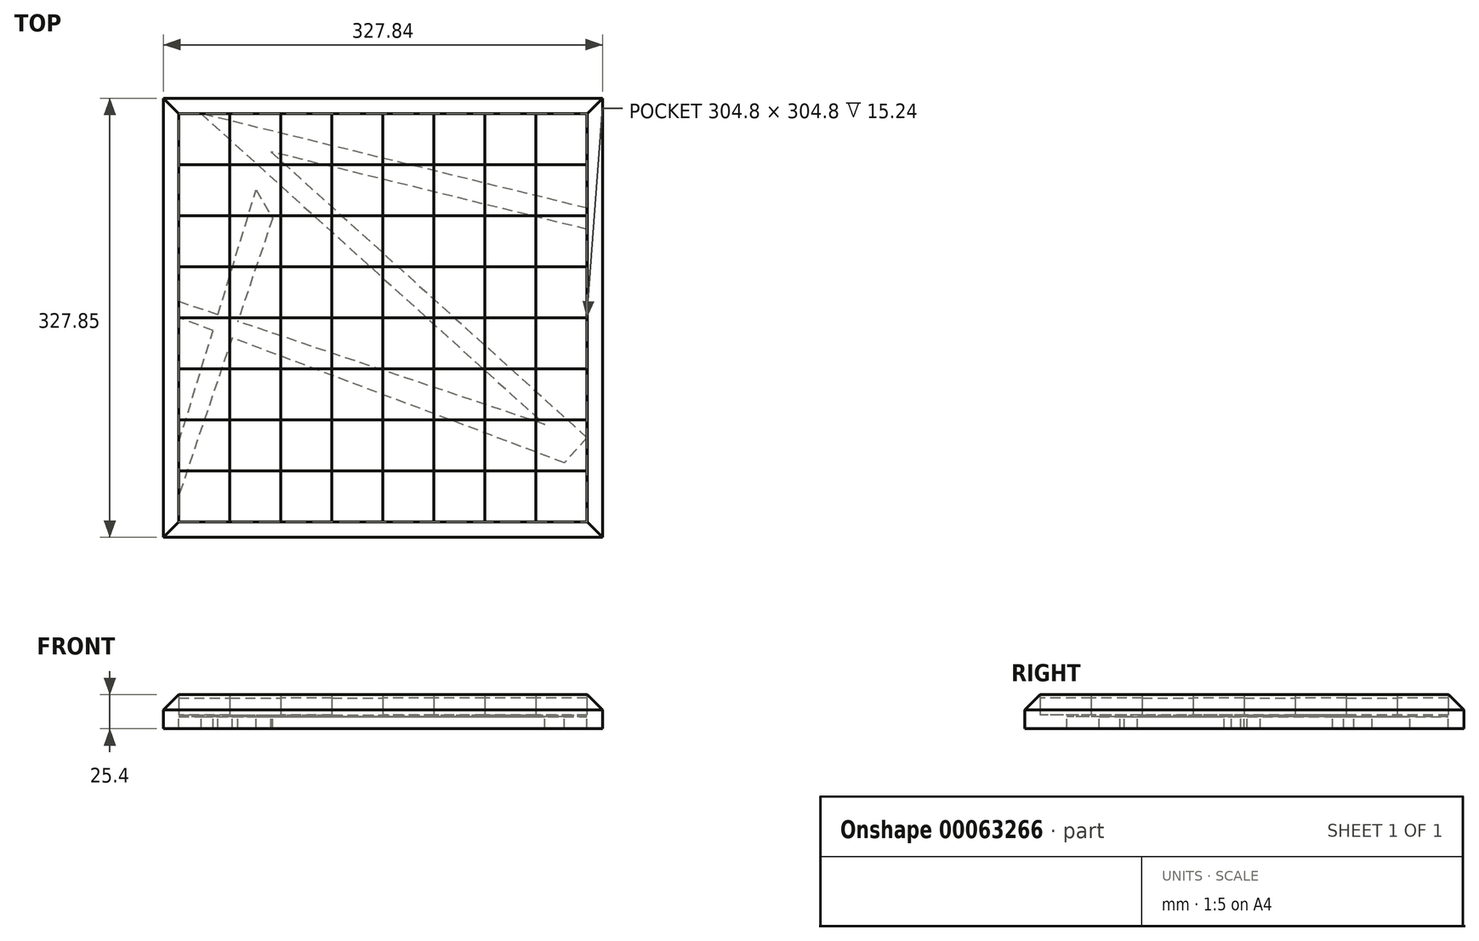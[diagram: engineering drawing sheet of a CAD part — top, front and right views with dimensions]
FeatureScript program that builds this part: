
annotation { "Feature Type Name" : "Feature", "Feature Type Description" : "" }
export const myFeature = defineFeature(function(context is Context, id is Id, definition is map)
    precondition{}
    {
        {
            var Q0;
            Q0=qCreatedBy(makeId("Top.planeOp"),FACE);
            var sketch = newSketch(context, id + "F0", { "sketchPlane" : qUnion([Q0])});
            skLineSegment(sketch, "E0", {"start": v(-203.2, 101.88) * mm, "end": v(101.6, 101.88) * mm});
            skLineSegment(sketch, "E1", {"start": v(101.6, 101.88) * mm, "end": v(101.6, -202.92) * mm});
            skLineSegment(sketch, "E2", {"start": v(101.6, -202.92) * mm, "end": v(-203.2, -202.92) * mm});
            skLineSegment(sketch, "E3", {"start": v(-203.2, -202.92) * mm, "end": v(-203.2, 101.88) * mm});
            skLineSegment(sketch, "E4", {"start": v(-165.1, 101.88) * mm, "end": v(-165.1, -202.92) * mm});
            skLineSegment(sketch, "E5", {"start": v(-127, -202.92) * mm, "end": v(-127, 101.88) * mm});
            skLineSegment(sketch, "E6", {"start": v(-88.9, 101.88) * mm, "end": v(-88.9, -202.92) * mm});
            skLineSegment(sketch, "E7", {"start": v(-50.8, 101.88) * mm, "end": v(-50.8, -202.92) * mm});
            skLineSegment(sketch, "E8", {"start": v(-12.7, -202.92) * mm, "end": v(-12.7, 101.88) * mm});
            skLineSegment(sketch, "E9", {"start": v(25.4, -202.92) * mm, "end": v(25.4, 101.88) * mm});
            skLineSegment(sketch, "E10", {"start": v(63.5, 101.88) * mm, "end": v(63.5, -202.92) * mm});
            skLineSegment(sketch, "E11", {"start": v(-203.2, 63.78) * mm, "end": v(101.6, 63.78) * mm});
            skLineSegment(sketch, "E12", {"start": v(-203.2, 25.68) * mm, "end": v(101.6, 25.68) * mm});
            skLineSegment(sketch, "E13", {"start": v(-203.2, -12.42) * mm, "end": v(101.6, -12.42) * mm});
            skLineSegment(sketch, "E14", {"start": v(101.6, -50.52) * mm, "end": v(-203.2, -50.52) * mm});
            skLineSegment(sketch, "E15", {"start": v(-203.2, -88.62) * mm, "end": v(101.6, -88.62) * mm});
            skLineSegment(sketch, "E16", {"start": v(101.6, -126.72) * mm, "end": v(-203.2, -126.72) * mm});
            skLineSegment(sketch, "E17", {"start": v(101.6, -164.82) * mm, "end": v(-203.2, -164.82) * mm});
            skSolve(sketch);
        }
        {
            var Q0;
            {var subQ0=sQuery(id+"F0.wireOp",EDGE,"E3");var subQ1=sQuery(id+"F0.wireOp",EDGE,"E0");var subQ2=makeQuery(id+"F0.imprint","INTERSECT",VERTEX,{"derivedFrom":[subQ1,subQ0]});Q0=makeQuery(id+"F0.imprint","IMPRINT",FACE,{"disambiguationData":[TD([[makeQuery(id+"F0.imprint","IMPRINT",EDGE,{"disambiguationData":[TD([[subQ2,-1.0]])],"derivedFrom":subQ1}),-1.0]])]});}
            var Q1;
            {var subQ0=sQuery(id+"F0.wireOp",EDGE,"E11");var subQ1=sQuery(id+"F0.wireOp",EDGE,"E4");var subQ2=makeQuery(id+"F0.imprint","INTERSECT",VERTEX,{"derivedFrom":[subQ1,subQ0]});Q1=makeQuery(id+"F0.imprint","IMPRINT",FACE,{"disambiguationData":[TD([[makeQuery(id+"F0.imprint","IMPRINT",EDGE,{"disambiguationData":[TD([[subQ2,-1.0]])],"derivedFrom":subQ1}),1.0]])]});}
            var Q2;
            {var subQ0=sQuery(id+"F0.wireOp",EDGE,"E5");var subQ1=sQuery(id+"F0.wireOp",EDGE,"E0");var subQ2=makeQuery(id+"F0.imprint","INTERSECT",VERTEX,{"derivedFrom":[subQ1,subQ0]});Q2=makeQuery(id+"F0.imprint","IMPRINT",FACE,{"disambiguationData":[TD([[makeQuery(id+"F0.imprint","IMPRINT",EDGE,{"disambiguationData":[TD([[subQ2,-1.0]])],"derivedFrom":subQ1}),-1.0]])]});}
            var Q3;
            {var subQ0=sQuery(id+"F0.wireOp",EDGE,"E11");var subQ1=sQuery(id+"F0.wireOp",EDGE,"E6");var subQ2=makeQuery(id+"F0.imprint","INTERSECT",VERTEX,{"derivedFrom":[subQ1,subQ0]});Q3=makeQuery(id+"F0.imprint","IMPRINT",FACE,{"disambiguationData":[TD([[makeQuery(id+"F0.imprint","IMPRINT",EDGE,{"disambiguationData":[TD([[subQ2,-1.0]])],"derivedFrom":subQ1}),1.0]])]});}
            var Q4;
            {var subQ0=sQuery(id+"F0.wireOp",EDGE,"E7");var subQ1=sQuery(id+"F0.wireOp",EDGE,"E0");var subQ2=makeQuery(id+"F0.imprint","INTERSECT",VERTEX,{"derivedFrom":[subQ1,subQ0]});Q4=makeQuery(id+"F0.imprint","IMPRINT",FACE,{"disambiguationData":[TD([[makeQuery(id+"F0.imprint","IMPRINT",EDGE,{"disambiguationData":[TD([[subQ2,-1.0]])],"derivedFrom":subQ1}),-1.0]])]});}
            var Q5;
            {var subQ0=sQuery(id+"F0.wireOp",EDGE,"E12");var subQ1=sQuery(id+"F0.wireOp",EDGE,"E8");var subQ2=makeQuery(id+"F0.imprint","INTERSECT",VERTEX,{"derivedFrom":[subQ1,subQ0]});Q5=makeQuery(id+"F0.imprint","IMPRINT",FACE,{"disambiguationData":[TD([[makeQuery(id+"F0.imprint","IMPRINT",EDGE,{"disambiguationData":[TD([[subQ2,-1.0]])],"derivedFrom":subQ1}),-1.0]])]});}
            var Q6;
            {var subQ0=sQuery(id+"F0.wireOp",EDGE,"E9");var subQ1=sQuery(id+"F0.wireOp",EDGE,"E0");var subQ2=makeQuery(id+"F0.imprint","INTERSECT",VERTEX,{"derivedFrom":[subQ1,subQ0]});Q6=makeQuery(id+"F0.imprint","IMPRINT",FACE,{"disambiguationData":[TD([[makeQuery(id+"F0.imprint","IMPRINT",EDGE,{"disambiguationData":[TD([[subQ2,-1.0]])],"derivedFrom":subQ1}),-1.0]])]});}
            var Q7;
            {var subQ0=sQuery(id+"F0.wireOp",EDGE,"E11");var subQ1=sQuery(id+"F0.wireOp",EDGE,"E1");var subQ2=makeQuery(id+"F0.imprint","INTERSECT",VERTEX,{"derivedFrom":[subQ1,subQ0]});Q7=makeQuery(id+"F0.imprint","IMPRINT",FACE,{"disambiguationData":[TD([[makeQuery(id+"F0.imprint","IMPRINT",EDGE,{"disambiguationData":[TD([[subQ2,-1.0]])],"derivedFrom":subQ1}),-1.0]])]});}
            var Q8;
            {var subQ0=sQuery(id+"F0.wireOp",EDGE,"E12");var subQ1=sQuery(id+"F0.wireOp",EDGE,"E3");var subQ2=makeQuery(id+"F0.imprint","INTERSECT",VERTEX,{"derivedFrom":[subQ1,subQ0]});Q8=makeQuery(id+"F0.imprint","IMPRINT",FACE,{"disambiguationData":[TD([[makeQuery(id+"F0.imprint","IMPRINT",EDGE,{"disambiguationData":[TD([[subQ2,1.0]])],"derivedFrom":subQ1}),-1.0]])]});}
            var Q9;
            {var subQ0=sQuery(id+"F0.wireOp",EDGE,"E13");var subQ1=sQuery(id+"F0.wireOp",EDGE,"E4");var subQ2=makeQuery(id+"F0.imprint","INTERSECT",VERTEX,{"derivedFrom":[subQ1,subQ0]});Q9=makeQuery(id+"F0.imprint","IMPRINT",FACE,{"disambiguationData":[TD([[makeQuery(id+"F0.imprint","IMPRINT",EDGE,{"disambiguationData":[TD([[subQ2,-1.0]])],"derivedFrom":subQ1}),1.0]])]});}
            var Q10;
            {var subQ0=sQuery(id+"F0.wireOp",EDGE,"E13");var subQ1=sQuery(id+"F0.wireOp",EDGE,"E5");var subQ2=makeQuery(id+"F0.imprint","INTERSECT",VERTEX,{"derivedFrom":[subQ1,subQ0]});Q10=makeQuery(id+"F0.imprint","IMPRINT",FACE,{"disambiguationData":[TD([[makeQuery(id+"F0.imprint","IMPRINT",EDGE,{"disambiguationData":[TD([[subQ2,-1.0]])],"derivedFrom":subQ1}),-1.0]])]});}
            var Q11;
            {var subQ0=sQuery(id+"F0.wireOp",EDGE,"E13");var subQ1=sQuery(id+"F0.wireOp",EDGE,"E6");var subQ2=makeQuery(id+"F0.imprint","INTERSECT",VERTEX,{"derivedFrom":[subQ1,subQ0]});Q11=makeQuery(id+"F0.imprint","IMPRINT",FACE,{"disambiguationData":[TD([[makeQuery(id+"F0.imprint","IMPRINT",EDGE,{"disambiguationData":[TD([[subQ2,-1.0]])],"derivedFrom":subQ1}),1.0]])]});}
            var Q12;
            {var subQ0=sQuery(id+"F0.wireOp",EDGE,"E12");var subQ1=sQuery(id+"F0.wireOp",EDGE,"E7");var subQ2=makeQuery(id+"F0.imprint","INTERSECT",VERTEX,{"derivedFrom":[subQ1,subQ0]});Q12=makeQuery(id+"F0.imprint","IMPRINT",FACE,{"disambiguationData":[TD([[makeQuery(id+"F0.imprint","IMPRINT",EDGE,{"disambiguationData":[TD([[subQ2,-1.0]])],"derivedFrom":subQ1}),1.0]])]});}
            var Q13;
            {var subQ0=sQuery(id+"F0.wireOp",EDGE,"E14");var subQ1=sQuery(id+"F0.wireOp",EDGE,"E8");var subQ2=makeQuery(id+"F0.imprint","INTERSECT",VERTEX,{"derivedFrom":[subQ1,subQ0]});Q13=makeQuery(id+"F0.imprint","IMPRINT",FACE,{"disambiguationData":[TD([[makeQuery(id+"F0.imprint","IMPRINT",EDGE,{"disambiguationData":[TD([[subQ2,-1.0]])],"derivedFrom":subQ1}),-1.0]])]});}
            var Q14;
            {var subQ0=sQuery(id+"F0.wireOp",EDGE,"E13");var subQ1=sQuery(id+"F0.wireOp",EDGE,"E9");var subQ2=makeQuery(id+"F0.imprint","INTERSECT",VERTEX,{"derivedFrom":[subQ1,subQ0]});Q14=makeQuery(id+"F0.imprint","IMPRINT",FACE,{"disambiguationData":[TD([[makeQuery(id+"F0.imprint","IMPRINT",EDGE,{"disambiguationData":[TD([[subQ2,-1.0]])],"derivedFrom":subQ1}),-1.0]])]});}
            var Q15;
            {var subQ0=sQuery(id+"F0.wireOp",EDGE,"E13");var subQ1=sQuery(id+"F0.wireOp",EDGE,"E1");var subQ2=makeQuery(id+"F0.imprint","INTERSECT",VERTEX,{"derivedFrom":[subQ1,subQ0]});Q15=makeQuery(id+"F0.imprint","IMPRINT",FACE,{"disambiguationData":[TD([[makeQuery(id+"F0.imprint","IMPRINT",EDGE,{"disambiguationData":[TD([[subQ2,-1.0]])],"derivedFrom":subQ1}),-1.0]])]});}
            var Q16;
            {var subQ0=sQuery(id+"F0.wireOp",EDGE,"E15");var subQ1=sQuery(id+"F0.wireOp",EDGE,"E9");var subQ2=makeQuery(id+"F0.imprint","INTERSECT",VERTEX,{"derivedFrom":[subQ1,subQ0]});Q16=makeQuery(id+"F0.imprint","IMPRINT",FACE,{"disambiguationData":[TD([[makeQuery(id+"F0.imprint","IMPRINT",EDGE,{"disambiguationData":[TD([[subQ2,-1.0]])],"derivedFrom":subQ1}),-1.0]])]});}
            var Q17;
            {var subQ0=sQuery(id+"F0.wireOp",EDGE,"E14");var subQ1=sQuery(id+"F0.wireOp",EDGE,"E7");var subQ2=makeQuery(id+"F0.imprint","INTERSECT",VERTEX,{"derivedFrom":[subQ1,subQ0]});Q17=makeQuery(id+"F0.imprint","IMPRINT",FACE,{"disambiguationData":[TD([[makeQuery(id+"F0.imprint","IMPRINT",EDGE,{"disambiguationData":[TD([[subQ2,-1.0]])],"derivedFrom":subQ1}),1.0]])]});}
            var Q18;
            {var subQ0=sQuery(id+"F0.wireOp",EDGE,"E15");var subQ1=sQuery(id+"F0.wireOp",EDGE,"E5");var subQ2=makeQuery(id+"F0.imprint","INTERSECT",VERTEX,{"derivedFrom":[subQ1,subQ0]});Q18=makeQuery(id+"F0.imprint","IMPRINT",FACE,{"disambiguationData":[TD([[makeQuery(id+"F0.imprint","IMPRINT",EDGE,{"disambiguationData":[TD([[subQ2,-1.0]])],"derivedFrom":subQ1}),-1.0]])]});}
            var Q19;
            {var subQ0=sQuery(id+"F0.wireOp",EDGE,"E14");var subQ1=sQuery(id+"F0.wireOp",EDGE,"E3");var subQ2=makeQuery(id+"F0.imprint","INTERSECT",VERTEX,{"derivedFrom":[subQ1,subQ0]});Q19=makeQuery(id+"F0.imprint","IMPRINT",FACE,{"disambiguationData":[TD([[makeQuery(id+"F0.imprint","IMPRINT",EDGE,{"disambiguationData":[TD([[subQ2,1.0]])],"derivedFrom":subQ1}),-1.0]])]});}
            var Q20;
            {var subQ0=sQuery(id+"F0.wireOp",EDGE,"E15");var subQ1=sQuery(id+"F0.wireOp",EDGE,"E4");var subQ2=makeQuery(id+"F0.imprint","INTERSECT",VERTEX,{"derivedFrom":[subQ1,subQ0]});Q20=makeQuery(id+"F0.imprint","IMPRINT",FACE,{"disambiguationData":[TD([[makeQuery(id+"F0.imprint","IMPRINT",EDGE,{"disambiguationData":[TD([[subQ2,-1.0]])],"derivedFrom":subQ1}),1.0]])]});}
            var Q21;
            {var subQ0=sQuery(id+"F0.wireOp",EDGE,"E15");var subQ1=sQuery(id+"F0.wireOp",EDGE,"E6");var subQ2=makeQuery(id+"F0.imprint","INTERSECT",VERTEX,{"derivedFrom":[subQ1,subQ0]});Q21=makeQuery(id+"F0.imprint","IMPRINT",FACE,{"disambiguationData":[TD([[makeQuery(id+"F0.imprint","IMPRINT",EDGE,{"disambiguationData":[TD([[subQ2,-1.0]])],"derivedFrom":subQ1}),1.0]])]});}
            var Q22;
            {var subQ0=sQuery(id+"F0.wireOp",EDGE,"E16");var subQ1=sQuery(id+"F0.wireOp",EDGE,"E8");var subQ2=makeQuery(id+"F0.imprint","INTERSECT",VERTEX,{"derivedFrom":[subQ1,subQ0]});Q22=makeQuery(id+"F0.imprint","IMPRINT",FACE,{"disambiguationData":[TD([[makeQuery(id+"F0.imprint","IMPRINT",EDGE,{"disambiguationData":[TD([[subQ2,-1.0]])],"derivedFrom":subQ1}),-1.0]])]});}
            var Q23;
            {var subQ0=sQuery(id+"F0.wireOp",EDGE,"E15");var subQ1=sQuery(id+"F0.wireOp",EDGE,"E1");var subQ2=makeQuery(id+"F0.imprint","INTERSECT",VERTEX,{"derivedFrom":[subQ1,subQ0]});Q23=makeQuery(id+"F0.imprint","IMPRINT",FACE,{"disambiguationData":[TD([[makeQuery(id+"F0.imprint","IMPRINT",EDGE,{"disambiguationData":[TD([[subQ2,-1.0]])],"derivedFrom":subQ1}),-1.0]])]});}
            var Q24;
            {var subQ0=sQuery(id+"F0.wireOp",EDGE,"E17");var subQ1=sQuery(id+"F0.wireOp",EDGE,"E9");var subQ2=makeQuery(id+"F0.imprint","INTERSECT",VERTEX,{"derivedFrom":[subQ1,subQ0]});Q24=makeQuery(id+"F0.imprint","IMPRINT",FACE,{"disambiguationData":[TD([[makeQuery(id+"F0.imprint","IMPRINT",EDGE,{"disambiguationData":[TD([[subQ2,-1.0]])],"derivedFrom":subQ1}),-1.0]])]});}
            var Q25;
            {var subQ0=sQuery(id+"F0.wireOp",EDGE,"E16");var subQ1=sQuery(id+"F0.wireOp",EDGE,"E7");var subQ2=makeQuery(id+"F0.imprint","INTERSECT",VERTEX,{"derivedFrom":[subQ1,subQ0]});Q25=makeQuery(id+"F0.imprint","IMPRINT",FACE,{"disambiguationData":[TD([[makeQuery(id+"F0.imprint","IMPRINT",EDGE,{"disambiguationData":[TD([[subQ2,-1.0]])],"derivedFrom":subQ1}),1.0]])]});}
            var Q26;
            {var subQ0=sQuery(id+"F0.wireOp",EDGE,"E17");var subQ1=sQuery(id+"F0.wireOp",EDGE,"E5");var subQ2=makeQuery(id+"F0.imprint","INTERSECT",VERTEX,{"derivedFrom":[subQ1,subQ0]});Q26=makeQuery(id+"F0.imprint","IMPRINT",FACE,{"disambiguationData":[TD([[makeQuery(id+"F0.imprint","IMPRINT",EDGE,{"disambiguationData":[TD([[subQ2,-1.0]])],"derivedFrom":subQ1}),-1.0]])]});}
            var Q27;
            {var subQ0=sQuery(id+"F0.wireOp",EDGE,"E16");var subQ1=sQuery(id+"F0.wireOp",EDGE,"E3");var subQ2=makeQuery(id+"F0.imprint","INTERSECT",VERTEX,{"derivedFrom":[subQ1,subQ0]});Q27=makeQuery(id+"F0.imprint","IMPRINT",FACE,{"disambiguationData":[TD([[makeQuery(id+"F0.imprint","IMPRINT",EDGE,{"disambiguationData":[TD([[subQ2,1.0]])],"derivedFrom":subQ1}),-1.0]])]});}
            var Q28;
            {var subQ0=sQuery(id+"F0.wireOp",EDGE,"E4");var subQ1=sQuery(id+"F0.wireOp",EDGE,"E2");var subQ2=makeQuery(id+"F0.imprint","INTERSECT",VERTEX,{"derivedFrom":[subQ1,subQ0]});Q28=makeQuery(id+"F0.imprint","IMPRINT",FACE,{"disambiguationData":[TD([[makeQuery(id+"F0.imprint","IMPRINT",EDGE,{"disambiguationData":[TD([[subQ2,1.0]])],"derivedFrom":subQ1}),-1.0]])]});}
            var Q29;
            {var subQ0=sQuery(id+"F0.wireOp",EDGE,"E6");var subQ1=sQuery(id+"F0.wireOp",EDGE,"E2");var subQ2=makeQuery(id+"F0.imprint","INTERSECT",VERTEX,{"derivedFrom":[subQ1,subQ0]});Q29=makeQuery(id+"F0.imprint","IMPRINT",FACE,{"disambiguationData":[TD([[makeQuery(id+"F0.imprint","IMPRINT",EDGE,{"disambiguationData":[TD([[subQ2,1.0]])],"derivedFrom":subQ1}),-1.0]])]});}
            var Q30;
            {var subQ0=sQuery(id+"F0.wireOp",EDGE,"E8");var subQ1=sQuery(id+"F0.wireOp",EDGE,"E2");var subQ2=makeQuery(id+"F0.imprint","INTERSECT",VERTEX,{"derivedFrom":[subQ1,subQ0]});Q30=makeQuery(id+"F0.imprint","IMPRINT",FACE,{"disambiguationData":[TD([[makeQuery(id+"F0.imprint","IMPRINT",EDGE,{"disambiguationData":[TD([[subQ2,1.0]])],"derivedFrom":subQ1}),-1.0]])]});}
            var Q31;
            {var subQ0=sQuery(id+"F0.wireOp",EDGE,"E2");var subQ1=sQuery(id+"F0.wireOp",EDGE,"E1");var subQ2=makeQuery(id+"F0.imprint","INTERSECT",VERTEX,{"derivedFrom":[subQ1,subQ0]});Q31=makeQuery(id+"F0.imprint","IMPRINT",FACE,{"disambiguationData":[TD([[makeQuery(id+"F0.imprint","IMPRINT",EDGE,{"disambiguationData":[TD([[subQ2,1.0]])],"derivedFrom":subQ1}),-1.0]])]});}
            extrude(context, id + "F1", {"entities" : qUnion([Q0, Q1, Q2, Q3, Q4, Q5, Q6, Q7, Q8, Q9, Q10, Q11, Q12, Q13, Q14, Q15, Q16, Q17, Q18, Q19, Q20, Q21, Q22, Q23, Q24, Q25, Q26, Q27, Q28, Q29, Q30, Q31]), "depth" : 12.7 * mm});
        }
        {
            var Q0;
            {var subQ0=sQuery(id+"F0.wireOp",EDGE,"E4");var subQ1=sQuery(id+"F0.wireOp",EDGE,"E0");var subQ2=makeQuery(id+"F0.imprint","INTERSECT",VERTEX,{"derivedFrom":[subQ1,subQ0]});Q0=makeQuery(id+"F0.imprint","IMPRINT",FACE,{"disambiguationData":[TD([[makeQuery(id+"F0.imprint","IMPRINT",EDGE,{"disambiguationData":[TD([[subQ2,-1.0]])],"derivedFrom":subQ1}),-1.0]])]});}
            var Q1;
            {var subQ0=sQuery(id+"F0.wireOp",EDGE,"E11");var subQ1=sQuery(id+"F0.wireOp",EDGE,"E3");var subQ2=makeQuery(id+"F0.imprint","INTERSECT",VERTEX,{"derivedFrom":[subQ1,subQ0]});Q1=makeQuery(id+"F0.imprint","IMPRINT",FACE,{"disambiguationData":[TD([[makeQuery(id+"F0.imprint","IMPRINT",EDGE,{"disambiguationData":[TD([[subQ2,1.0]])],"derivedFrom":subQ1}),-1.0]])]});}
            var Q2;
            {var subQ0=sQuery(id+"F0.wireOp",EDGE,"E12");var subQ1=sQuery(id+"F0.wireOp",EDGE,"E4");var subQ2=makeQuery(id+"F0.imprint","INTERSECT",VERTEX,{"derivedFrom":[subQ1,subQ0]});Q2=makeQuery(id+"F0.imprint","IMPRINT",FACE,{"disambiguationData":[TD([[makeQuery(id+"F0.imprint","IMPRINT",EDGE,{"disambiguationData":[TD([[subQ2,-1.0]])],"derivedFrom":subQ1}),1.0]])]});}
            var Q3;
            {var subQ0=sQuery(id+"F0.wireOp",EDGE,"E12");var subQ1=sQuery(id+"F0.wireOp",EDGE,"E5");var subQ2=makeQuery(id+"F0.imprint","INTERSECT",VERTEX,{"derivedFrom":[subQ1,subQ0]});Q3=makeQuery(id+"F0.imprint","IMPRINT",FACE,{"disambiguationData":[TD([[makeQuery(id+"F0.imprint","IMPRINT",EDGE,{"disambiguationData":[TD([[subQ2,-1.0]])],"derivedFrom":subQ1}),-1.0]])]});}
            var Q4;
            {var subQ0=sQuery(id+"F0.wireOp",EDGE,"E6");var subQ1=sQuery(id+"F0.wireOp",EDGE,"E0");var subQ2=makeQuery(id+"F0.imprint","INTERSECT",VERTEX,{"derivedFrom":[subQ1,subQ0]});Q4=makeQuery(id+"F0.imprint","IMPRINT",FACE,{"disambiguationData":[TD([[makeQuery(id+"F0.imprint","IMPRINT",EDGE,{"disambiguationData":[TD([[subQ2,-1.0]])],"derivedFrom":subQ1}),-1.0]])]});}
            var Q5;
            {var subQ0=sQuery(id+"F0.wireOp",EDGE,"E12");var subQ1=sQuery(id+"F0.wireOp",EDGE,"E6");var subQ2=makeQuery(id+"F0.imprint","INTERSECT",VERTEX,{"derivedFrom":[subQ1,subQ0]});Q5=makeQuery(id+"F0.imprint","IMPRINT",FACE,{"disambiguationData":[TD([[makeQuery(id+"F0.imprint","IMPRINT",EDGE,{"disambiguationData":[TD([[subQ2,-1.0]])],"derivedFrom":subQ1}),1.0]])]});}
            var Q6;
            {var subQ0=sQuery(id+"F0.wireOp",EDGE,"E11");var subQ1=sQuery(id+"F0.wireOp",EDGE,"E7");var subQ2=makeQuery(id+"F0.imprint","INTERSECT",VERTEX,{"derivedFrom":[subQ1,subQ0]});Q6=makeQuery(id+"F0.imprint","IMPRINT",FACE,{"disambiguationData":[TD([[makeQuery(id+"F0.imprint","IMPRINT",EDGE,{"disambiguationData":[TD([[subQ2,-1.0]])],"derivedFrom":subQ1}),1.0]])]});}
            var Q7;
            {var subQ0=sQuery(id+"F0.wireOp",EDGE,"E8");var subQ1=sQuery(id+"F0.wireOp",EDGE,"E0");var subQ2=makeQuery(id+"F0.imprint","INTERSECT",VERTEX,{"derivedFrom":[subQ1,subQ0]});Q7=makeQuery(id+"F0.imprint","IMPRINT",FACE,{"disambiguationData":[TD([[makeQuery(id+"F0.imprint","IMPRINT",EDGE,{"disambiguationData":[TD([[subQ2,-1.0]])],"derivedFrom":subQ1}),-1.0]])]});}
            var Q8;
            {var subQ0=sQuery(id+"F0.wireOp",EDGE,"E12");var subQ1=sQuery(id+"F0.wireOp",EDGE,"E9");var subQ2=makeQuery(id+"F0.imprint","INTERSECT",VERTEX,{"derivedFrom":[subQ1,subQ0]});Q8=makeQuery(id+"F0.imprint","IMPRINT",FACE,{"disambiguationData":[TD([[makeQuery(id+"F0.imprint","IMPRINT",EDGE,{"disambiguationData":[TD([[subQ2,-1.0]])],"derivedFrom":subQ1}),-1.0]])]});}
            var Q9;
            {var subQ0=sQuery(id+"F0.wireOp",EDGE,"E13");var subQ1=sQuery(id+"F0.wireOp",EDGE,"E8");var subQ2=makeQuery(id+"F0.imprint","INTERSECT",VERTEX,{"derivedFrom":[subQ1,subQ0]});Q9=makeQuery(id+"F0.imprint","IMPRINT",FACE,{"disambiguationData":[TD([[makeQuery(id+"F0.imprint","IMPRINT",EDGE,{"disambiguationData":[TD([[subQ2,-1.0]])],"derivedFrom":subQ1}),-1.0]])]});}
            var Q10;
            {var subQ0=sQuery(id+"F0.wireOp",EDGE,"E1");var subQ1=sQuery(id+"F0.wireOp",EDGE,"E0");var subQ2=makeQuery(id+"F0.imprint","INTERSECT",VERTEX,{"derivedFrom":[subQ1,subQ0]});Q10=makeQuery(id+"F0.imprint","IMPRINT",FACE,{"disambiguationData":[TD([[makeQuery(id+"F0.imprint","IMPRINT",EDGE,{"disambiguationData":[TD([[subQ2,1.0]])],"derivedFrom":subQ1}),-1.0]])]});}
            var Q11;
            {var subQ0=sQuery(id+"F0.wireOp",EDGE,"E12");var subQ1=sQuery(id+"F0.wireOp",EDGE,"E1");var subQ2=makeQuery(id+"F0.imprint","INTERSECT",VERTEX,{"derivedFrom":[subQ1,subQ0]});Q11=makeQuery(id+"F0.imprint","IMPRINT",FACE,{"disambiguationData":[TD([[makeQuery(id+"F0.imprint","IMPRINT",EDGE,{"disambiguationData":[TD([[subQ2,-1.0]])],"derivedFrom":subQ1}),-1.0]])]});}
            var Q12;
            {var subQ0=sQuery(id+"F0.wireOp",EDGE,"E14");var subQ1=sQuery(id+"F0.wireOp",EDGE,"E1");var subQ2=makeQuery(id+"F0.imprint","INTERSECT",VERTEX,{"derivedFrom":[subQ1,subQ0]});Q12=makeQuery(id+"F0.imprint","IMPRINT",FACE,{"disambiguationData":[TD([[makeQuery(id+"F0.imprint","IMPRINT",EDGE,{"disambiguationData":[TD([[subQ2,-1.0]])],"derivedFrom":subQ1}),-1.0]])]});}
            var Q13;
            {var subQ0=sQuery(id+"F0.wireOp",EDGE,"E14");var subQ1=sQuery(id+"F0.wireOp",EDGE,"E9");var subQ2=makeQuery(id+"F0.imprint","INTERSECT",VERTEX,{"derivedFrom":[subQ1,subQ0]});Q13=makeQuery(id+"F0.imprint","IMPRINT",FACE,{"disambiguationData":[TD([[makeQuery(id+"F0.imprint","IMPRINT",EDGE,{"disambiguationData":[TD([[subQ2,-1.0]])],"derivedFrom":subQ1}),-1.0]])]});}
            var Q14;
            {var subQ0=sQuery(id+"F0.wireOp",EDGE,"E15");var subQ1=sQuery(id+"F0.wireOp",EDGE,"E8");var subQ2=makeQuery(id+"F0.imprint","INTERSECT",VERTEX,{"derivedFrom":[subQ1,subQ0]});Q14=makeQuery(id+"F0.imprint","IMPRINT",FACE,{"disambiguationData":[TD([[makeQuery(id+"F0.imprint","IMPRINT",EDGE,{"disambiguationData":[TD([[subQ2,-1.0]])],"derivedFrom":subQ1}),-1.0]])]});}
            var Q15;
            {var subQ0=sQuery(id+"F0.wireOp",EDGE,"E13");var subQ1=sQuery(id+"F0.wireOp",EDGE,"E7");var subQ2=makeQuery(id+"F0.imprint","INTERSECT",VERTEX,{"derivedFrom":[subQ1,subQ0]});Q15=makeQuery(id+"F0.imprint","IMPRINT",FACE,{"disambiguationData":[TD([[makeQuery(id+"F0.imprint","IMPRINT",EDGE,{"disambiguationData":[TD([[subQ2,-1.0]])],"derivedFrom":subQ1}),1.0]])]});}
            var Q16;
            {var subQ0=sQuery(id+"F0.wireOp",EDGE,"E14");var subQ1=sQuery(id+"F0.wireOp",EDGE,"E6");var subQ2=makeQuery(id+"F0.imprint","INTERSECT",VERTEX,{"derivedFrom":[subQ1,subQ0]});Q16=makeQuery(id+"F0.imprint","IMPRINT",FACE,{"disambiguationData":[TD([[makeQuery(id+"F0.imprint","IMPRINT",EDGE,{"disambiguationData":[TD([[subQ2,-1.0]])],"derivedFrom":subQ1}),1.0]])]});}
            var Q17;
            {var subQ0=sQuery(id+"F0.wireOp",EDGE,"E14");var subQ1=sQuery(id+"F0.wireOp",EDGE,"E5");var subQ2=makeQuery(id+"F0.imprint","INTERSECT",VERTEX,{"derivedFrom":[subQ1,subQ0]});Q17=makeQuery(id+"F0.imprint","IMPRINT",FACE,{"disambiguationData":[TD([[makeQuery(id+"F0.imprint","IMPRINT",EDGE,{"disambiguationData":[TD([[subQ2,-1.0]])],"derivedFrom":subQ1}),-1.0]])]});}
            var Q18;
            {var subQ0=sQuery(id+"F0.wireOp",EDGE,"E14");var subQ1=sQuery(id+"F0.wireOp",EDGE,"E4");var subQ2=makeQuery(id+"F0.imprint","INTERSECT",VERTEX,{"derivedFrom":[subQ1,subQ0]});Q18=makeQuery(id+"F0.imprint","IMPRINT",FACE,{"disambiguationData":[TD([[makeQuery(id+"F0.imprint","IMPRINT",EDGE,{"disambiguationData":[TD([[subQ2,-1.0]])],"derivedFrom":subQ1}),1.0]])]});}
            var Q19;
            {var subQ0=sQuery(id+"F0.wireOp",EDGE,"E13");var subQ1=sQuery(id+"F0.wireOp",EDGE,"E3");var subQ2=makeQuery(id+"F0.imprint","INTERSECT",VERTEX,{"derivedFrom":[subQ1,subQ0]});Q19=makeQuery(id+"F0.imprint","IMPRINT",FACE,{"disambiguationData":[TD([[makeQuery(id+"F0.imprint","IMPRINT",EDGE,{"disambiguationData":[TD([[subQ2,1.0]])],"derivedFrom":subQ1}),-1.0]])]});}
            var Q20;
            {var subQ0=sQuery(id+"F0.wireOp",EDGE,"E15");var subQ1=sQuery(id+"F0.wireOp",EDGE,"E3");var subQ2=makeQuery(id+"F0.imprint","INTERSECT",VERTEX,{"derivedFrom":[subQ1,subQ0]});Q20=makeQuery(id+"F0.imprint","IMPRINT",FACE,{"disambiguationData":[TD([[makeQuery(id+"F0.imprint","IMPRINT",EDGE,{"disambiguationData":[TD([[subQ2,1.0]])],"derivedFrom":subQ1}),-1.0]])]});}
            var Q21;
            {var subQ0=sQuery(id+"F0.wireOp",EDGE,"E16");var subQ1=sQuery(id+"F0.wireOp",EDGE,"E4");var subQ2=makeQuery(id+"F0.imprint","INTERSECT",VERTEX,{"derivedFrom":[subQ1,subQ0]});Q21=makeQuery(id+"F0.imprint","IMPRINT",FACE,{"disambiguationData":[TD([[makeQuery(id+"F0.imprint","IMPRINT",EDGE,{"disambiguationData":[TD([[subQ2,-1.0]])],"derivedFrom":subQ1}),1.0]])]});}
            var Q22;
            {var subQ0=sQuery(id+"F0.wireOp",EDGE,"E3");var subQ1=sQuery(id+"F0.wireOp",EDGE,"E2");var subQ2=makeQuery(id+"F0.imprint","INTERSECT",VERTEX,{"derivedFrom":[subQ1,subQ0]});Q22=makeQuery(id+"F0.imprint","IMPRINT",FACE,{"disambiguationData":[TD([[makeQuery(id+"F0.imprint","IMPRINT",EDGE,{"disambiguationData":[TD([[subQ2,1.0]])],"derivedFrom":subQ1}),-1.0]])]});}
            var Q23;
            {var subQ0=sQuery(id+"F0.wireOp",EDGE,"E16");var subQ1=sQuery(id+"F0.wireOp",EDGE,"E5");var subQ2=makeQuery(id+"F0.imprint","INTERSECT",VERTEX,{"derivedFrom":[subQ1,subQ0]});Q23=makeQuery(id+"F0.imprint","IMPRINT",FACE,{"disambiguationData":[TD([[makeQuery(id+"F0.imprint","IMPRINT",EDGE,{"disambiguationData":[TD([[subQ2,-1.0]])],"derivedFrom":subQ1}),-1.0]])]});}
            var Q24;
            {var subQ0=sQuery(id+"F0.wireOp",EDGE,"E16");var subQ1=sQuery(id+"F0.wireOp",EDGE,"E6");var subQ2=makeQuery(id+"F0.imprint","INTERSECT",VERTEX,{"derivedFrom":[subQ1,subQ0]});Q24=makeQuery(id+"F0.imprint","IMPRINT",FACE,{"disambiguationData":[TD([[makeQuery(id+"F0.imprint","IMPRINT",EDGE,{"disambiguationData":[TD([[subQ2,-1.0]])],"derivedFrom":subQ1}),1.0]])]});}
            var Q25;
            {var subQ0=sQuery(id+"F0.wireOp",EDGE,"E5");var subQ1=sQuery(id+"F0.wireOp",EDGE,"E2");var subQ2=makeQuery(id+"F0.imprint","INTERSECT",VERTEX,{"derivedFrom":[subQ1,subQ0]});Q25=makeQuery(id+"F0.imprint","IMPRINT",FACE,{"disambiguationData":[TD([[makeQuery(id+"F0.imprint","IMPRINT",EDGE,{"disambiguationData":[TD([[subQ2,1.0]])],"derivedFrom":subQ1}),-1.0]])]});}
            var Q26;
            {var subQ0=sQuery(id+"F0.wireOp",EDGE,"E7");var subQ1=sQuery(id+"F0.wireOp",EDGE,"E2");var subQ2=makeQuery(id+"F0.imprint","INTERSECT",VERTEX,{"derivedFrom":[subQ1,subQ0]});Q26=makeQuery(id+"F0.imprint","IMPRINT",FACE,{"disambiguationData":[TD([[makeQuery(id+"F0.imprint","IMPRINT",EDGE,{"disambiguationData":[TD([[subQ2,1.0]])],"derivedFrom":subQ1}),-1.0]])]});}
            var Q27;
            {var subQ0=sQuery(id+"F0.wireOp",EDGE,"E17");var subQ1=sQuery(id+"F0.wireOp",EDGE,"E8");var subQ2=makeQuery(id+"F0.imprint","INTERSECT",VERTEX,{"derivedFrom":[subQ1,subQ0]});Q27=makeQuery(id+"F0.imprint","IMPRINT",FACE,{"disambiguationData":[TD([[makeQuery(id+"F0.imprint","IMPRINT",EDGE,{"disambiguationData":[TD([[subQ2,-1.0]])],"derivedFrom":subQ1}),-1.0]])]});}
            var Q28;
            {var subQ0=sQuery(id+"F0.wireOp",EDGE,"E15");var subQ1=sQuery(id+"F0.wireOp",EDGE,"E7");var subQ2=makeQuery(id+"F0.imprint","INTERSECT",VERTEX,{"derivedFrom":[subQ1,subQ0]});Q28=makeQuery(id+"F0.imprint","IMPRINT",FACE,{"disambiguationData":[TD([[makeQuery(id+"F0.imprint","IMPRINT",EDGE,{"disambiguationData":[TD([[subQ2,-1.0]])],"derivedFrom":subQ1}),1.0]])]});}
            var Q29;
            {var subQ0=sQuery(id+"F0.wireOp",EDGE,"E16");var subQ1=sQuery(id+"F0.wireOp",EDGE,"E9");var subQ2=makeQuery(id+"F0.imprint","INTERSECT",VERTEX,{"derivedFrom":[subQ1,subQ0]});Q29=makeQuery(id+"F0.imprint","IMPRINT",FACE,{"disambiguationData":[TD([[makeQuery(id+"F0.imprint","IMPRINT",EDGE,{"disambiguationData":[TD([[subQ2,-1.0]])],"derivedFrom":subQ1}),-1.0]])]});}
            var Q30;
            {var subQ0=sQuery(id+"F0.wireOp",EDGE,"E16");var subQ1=sQuery(id+"F0.wireOp",EDGE,"E1");var subQ2=makeQuery(id+"F0.imprint","INTERSECT",VERTEX,{"derivedFrom":[subQ1,subQ0]});Q30=makeQuery(id+"F0.imprint","IMPRINT",FACE,{"disambiguationData":[TD([[makeQuery(id+"F0.imprint","IMPRINT",EDGE,{"disambiguationData":[TD([[subQ2,-1.0]])],"derivedFrom":subQ1}),-1.0]])]});}
            var Q31;
            {var subQ0=sQuery(id+"F0.wireOp",EDGE,"E9");var subQ1=sQuery(id+"F0.wireOp",EDGE,"E2");var subQ2=makeQuery(id+"F0.imprint","INTERSECT",VERTEX,{"derivedFrom":[subQ1,subQ0]});Q31=makeQuery(id+"F0.imprint","IMPRINT",FACE,{"disambiguationData":[TD([[makeQuery(id+"F0.imprint","IMPRINT",EDGE,{"disambiguationData":[TD([[subQ2,1.0]])],"derivedFrom":subQ1}),-1.0]])]});}
            extrude(context, id + "F2", {"entities" : qUnion([Q0, Q1, Q2, Q3, Q4, Q5, Q6, Q7, Q8, Q9, Q10, Q11, Q12, Q13, Q14, Q15, Q16, Q17, Q18, Q19, Q20, Q21, Q22, Q23, Q24, Q25, Q26, Q27, Q28, Q29, Q30, Q31]), "depth" : 15.24 * mm});
        }
        {
            var Q0;
            Q0=makeQuery(id+"F1.opExtrude","CAP_FACE",FACE,{"disambiguationData":[OSD([sQuery(id+"F0.wireOp",EDGE,"E7"),sQuery(id+"F0.wireOp",EDGE,"E8"),sQuery(id+"F0.wireOp",EDGE,"E12"),sQuery(id+"F0.wireOp",EDGE,"E13")])],"isStart":true});
            var sketch = newSketch(context, id + "F3", { "sketchPlane" : qUnion([Q0])});
            skPoint(sketch, "E18.0", {"position": v(-203.2, -101.88) * mm});
            skPoint(sketch, "E19.0", {"position": v(101.6, -101.88) * mm});
            skPoint(sketch, "E20.0", {"position": v(101.6, 202.92) * mm});
            skPoint(sketch, "E21.0", {"position": v(-203.2, 202.92) * mm});
            skLineSegment(sketch, "E22.bottom", {"start": v(-203.2, -101.88) * mm, "end": v(101.6, -101.88) * mm});
            skLineSegment(sketch, "E22.top", {"start": v(-203.2, 202.92) * mm, "end": v(101.6, 202.92) * mm});
            skLineSegment(sketch, "E22.left", {"start": v(-203.2, -101.88) * mm, "end": v(-203.2, 202.92) * mm});
            skLineSegment(sketch, "E22.right", {"start": v(101.6, -101.88) * mm, "end": v(101.6, 202.92) * mm});
            skLineSegment(sketch, "E23.0", {"start": v(-214.72, -113.4) * mm, "end": v(-214.72, 214.45) * mm});
            skLineSegment(sketch, "E23.1", {"start": v(-214.72, -113.4) * mm, "end": v(113.12, -113.4) * mm});
            skLineSegment(sketch, "E23.2", {"start": v(113.12, -113.4) * mm, "end": v(113.12, 214.45) * mm});
            skLineSegment(sketch, "E23.3", {"start": v(-214.72, 214.45) * mm, "end": v(113.12, 214.45) * mm});
            skSolve(sketch);
        }
        {
            var Q0;
            Q0 = qSketchRegion(id + "F3", true);
            extrude(context, id + "F4", {"entities" : qUnion([Q0]), "oppositeDirection" : true, "depth" : 15.24 * mm, "hasSecondDirection" : true, "secondDirectionOppositeDirection" : false, "secondDirectionDepth" : 10.16 * mm});
        }
        {
            var Q0;
            Q0=makeQuery(id+"F4.opExtrude","CAP_EDGE",EDGE,{"disambiguationData":[OSD([sQuery(id+"F3.wireOp",EDGE,"E23.0")])],"isStart":false});
            var Q1;
            Q1=makeQuery(id+"F4.opExtrude","CAP_EDGE",EDGE,{"disambiguationData":[OSD([sQuery(id+"F3.wireOp",EDGE,"E23.1")])],"isStart":false});
            var Q2;
            Q2=makeQuery(id+"F4.opExtrude","CAP_EDGE",EDGE,{"disambiguationData":[OSD([sQuery(id+"F3.wireOp",EDGE,"E23.2")])],"isStart":false});
            var Q3;
            Q3=makeQuery(id+"F4.opExtrude","CAP_EDGE",EDGE,{"disambiguationData":[OSD([sQuery(id+"F3.wireOp",EDGE,"E23.3")])],"isStart":false});
            chamfer(context, id + "F5", {"entities" : qUnion([Q0, Q1, Q2, Q3]), "width" : 11.43 * mm, "tangentPropagation" : true});
        }
        {
            var Q0;
            Q0=makeQuery(id+"F3.imprint","IMPRINT",FACE,{"disambiguationData":[TD([[makeQuery(id+"F3.imprint","IMPRINT",EDGE,{"derivedFrom":sQuery(id+"F3.wireOp",EDGE,"E22.bottom")}),1.0]])]});
            var Q1;
            {var subQ0=sQuery(id+"F0.wireOp",EDGE,"E12");var subQ1=sQuery(id+"F0.wireOp",EDGE,"E7");var subQ2=makeQuery(id+"F0.imprint","INTERSECT",VERTEX,{"derivedFrom":[subQ1,subQ0]});Q1=makeQuery(id+"F3.imprint","IMPRINT",FACE,{"disambiguationData":[TD([[makeQuery(id+"F3.imprint","IMPRINT",EDGE,{"derivedFrom":makeQuery(id+"F1.opExtrude","CAP_EDGE",EDGE,{"disambiguationData":[OSD([subQ1]),TDD([makeQuery(id+"F0.imprint","IMPRINT",EDGE,{"disambiguationData":[TD([[subQ2,-1.0]])],"derivedFrom":subQ1})])],"isStart":true})}),-1.0]])]});}
            extrude(context, id + "F6", {"entities" : qUnion([Q0, Q1]), "depth" : 1.27 * mm});
        }
        {
            var Q0;
            Q0=makeQuery(id+"F6.opExtrude","CAP_FACE",FACE,{"disambiguationData":[OSD([sQuery(id+"F3.wireOp",EDGE,"E22.bottom"),sQuery(id+"F3.wireOp",EDGE,"E22.top"),sQuery(id+"F3.wireOp",EDGE,"E22.left"),sQuery(id+"F3.wireOp",EDGE,"E22.right")])],"isStart":false});
            var sketch = newSketch(context, id + "F7", { "sketchPlane" : qUnion([Q0])});
            skLineSegment(sketch, "E24", {"start": v(101.6, -31.27) * mm, "end": v(-186.66, -101.88) * mm});
            skLineSegment(sketch, "E25", {"start": v(-186.66, -101.88) * mm, "end": v(70, 130.26) * mm});
            skLineSegment(sketch, "E26", {"start": v(101.6, -15.53) * mm, "end": v(-134.37, -73.33) * mm});
            skLineSegment(sketch, "E27", {"start": v(-134.37, -73.33) * mm, "end": v(101.6, 140.1) * mm});
            skLineSegment(sketch, "E28", {"start": v(101.6, 140.1) * mm, "end": v(84.65, 158.83) * mm});
            skLineSegment(sketch, "E29", {"start": v(70, 130.26) * mm, "end": v(-203.2, 38.54) * mm});
            skLineSegment(sketch, "E30", {"start": v(84.65, 158.83) * mm, "end": v(-203.2, 50.52) * mm});
            skLineSegment(sketch, "E31", {"start": v(-203.2, 143.26) * mm, "end": v(-145.6, -44.96) * mm});
            skLineSegment(sketch, "E32", {"start": v(-145.6, -44.96) * mm, "end": v(-133.27, -23.74) * mm});
            skLineSegment(sketch, "E33", {"start": v(-133.27, -23.74) * mm, "end": v(-203.2, 182.96) * mm});
            skSolve(sketch);
        }
        {
            var Q0;
            {var subQ0=sQuery(id+"F7.wireOp",EDGE,"E24");Q0=makeQuery(id+"F7.imprint","IMPRINT",FACE,{"disambiguationData":[TD([[makeQuery(id+"F7.imprint","IMPRINT",EDGE,{"derivedFrom":subQ0}),1.0]])]});}
            var Q1;
            {var subQ8=sQuery(id+"F7.wireOp",EDGE,"E25");Q1=makeQuery(id+"F7.imprint","IMPRINT",FACE,{"disambiguationData":[TD([[makeQuery(id+"F7.imprint","IMPRINT",EDGE,{"derivedFrom":subQ8}),1.0]])]});}
            var Q2;
            {var subQ0=sQuery(id+"F7.wireOp",EDGE,"E26");Q2=makeQuery(id+"F7.imprint","IMPRINT",FACE,{"disambiguationData":[TD([[makeQuery(id+"F7.imprint","IMPRINT",EDGE,{"derivedFrom":subQ0}),-1.0]])]});}
            var Q3;
            {var subQ0=sQuery(id+"F7.wireOp",EDGE,"E30");var subQ1=makeQuery(id+"F6.opExtrude","CAP_EDGE",EDGE,{"disambiguationData":[OSD([sQuery(id+"F3.wireOp",EDGE,"E22.left")])],"isStart":false});var subQ2=makeQuery(id+"F7.imprint","INTERSECT",VERTEX,{"derivedFrom":[subQ1,subQ0]});Q3=makeQuery(id+"F7.imprint","IMPRINT",FACE,{"disambiguationData":[TD([[makeQuery(id+"F7.imprint","IMPRINT",EDGE,{"disambiguationData":[TD([[subQ2,1.0]])],"derivedFrom":subQ0}),-1.0]])]});}
            var Q4;
            {var subQ5=sQuery(id+"F7.wireOp",EDGE,"E28");Q4=makeQuery(id+"F7.imprint","IMPRINT",FACE,{"disambiguationData":[TD([[makeQuery(id+"F7.imprint","IMPRINT",EDGE,{"derivedFrom":subQ5}),-1.0]])]});}
            extrude(context, id + "F8", {"entities" : qUnion([Q0, Q1, Q2, Q3, Q4]), "operationType" : NewBodyOperationType.ADD, "depth" : 8.9 * mm});
        }
    });
